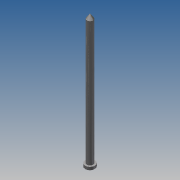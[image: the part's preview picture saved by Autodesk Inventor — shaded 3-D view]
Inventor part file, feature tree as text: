
AUTODESK INVENTOR PART (.ipt)
format: ipt  version: 2013 SP2 (Build 170200200, 200)  size: 91,136 bytes
history: native  units: in
note: dims shown in document units (in); Inventor stores cm internally (conversion verified against a paired STEP export)
features: sketch x4, extrude x2, plane x2, revolve x1, fillet x1
ambient origin geometry x8: Origin, YZ Plane, XZ Plane, XY Plane, X Axis, Y Axis, Z Axis, Center Point
bodies: Solid1 (feature_tree)
feature tree (10):
  extrude  "Extrusion1"  Depth=0.1in TaperAngle=0.0deg
  extrude  "Extrusion2"  Depth=4.0in TaperAngle=0.0deg
  sketch  "Sketch3"  dims[d11=-0.096in d12=90.0deg d13=0.02in]
  plane  "Work Plane2"
  revolve  "Revolution1"  Angle=90.0deg
  fillet  "Fillet1"  Radius=0.02in
  sketch  "Sketch1"  dims[d0=0.3in d3=0.1in d4=0.0in]
  sketch  "Sketch2"  dims[d5=0.192in d7=4.0in d8=0.0in]
  plane  "Work Plane1"
  sketch  "Sketch4"
